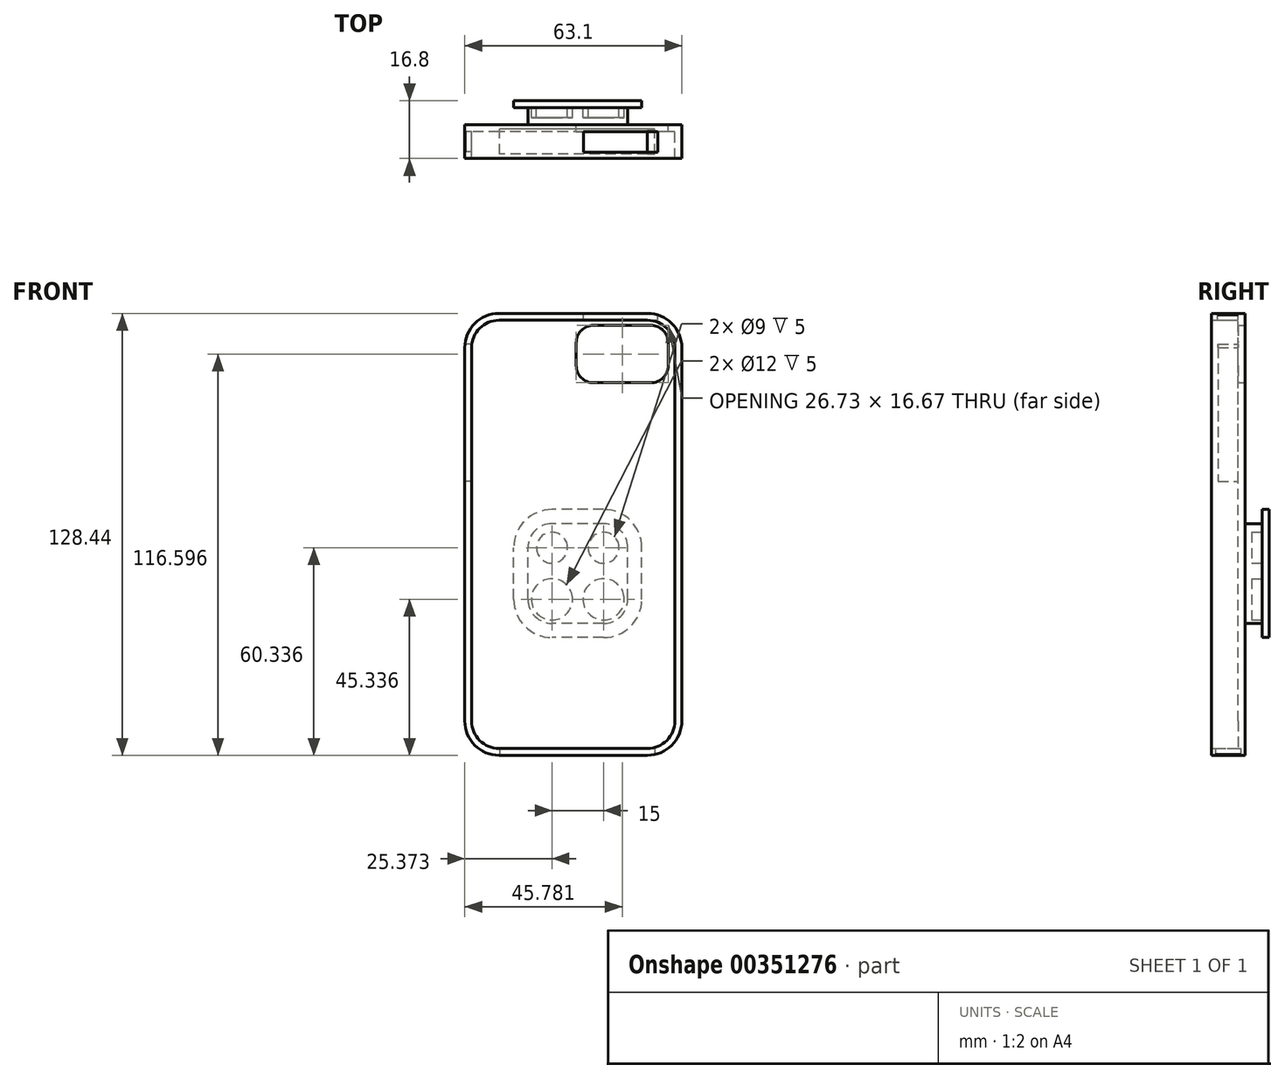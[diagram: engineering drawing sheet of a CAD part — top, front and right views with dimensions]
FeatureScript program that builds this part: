
annotation { "Feature Type Name" : "Feature", "Feature Type Description" : "" }
export const myFeature = defineFeature(function(context is Context, id is Id, definition is map)
    precondition{}
    {
        {
            var Q0;
            Q0=qCreatedBy(makeId("Front.planeOp"),FACE);
            var sketch = newSketch(context, id + "F0", { "sketchPlane" : qUnion([Q0])});
            skLineSegment(sketch, "E0.bottom", {"start": v(19.77, -64.98) * mm, "end": v(-23.33, -64.98) * mm});
            skLineSegment(sketch, "E0.top", {"start": v(19.77, 59.46) * mm, "end": v(-23.33, 59.46) * mm});
            skLineSegment(sketch, "E0.left", {"start": v(27.77, -56.98) * mm, "end": v(27.77, 51.46) * mm});
            skLineSegment(sketch, "E0.right", {"start": v(-31.33, -56.98) * mm, "end": v(-31.33, 51.46) * mm});
            skPoint(sketch, "E0.middle", {"position": v(0, 0) * mm});
            skArc(sketch, "E1.filletArc", {"start": v(-23.33, 59.46) * mm, "mid": v(-28.98, 57.12) * mm, "end": v(-31.33, 51.46) * mm});
            skArc(sketch, "E2.filletArc", {"start": v(27.77, 51.46) * mm, "mid": v(25.43, 57.12) * mm, "end": v(19.77, 59.46) * mm});
            skArc(sketch, "E3.filletArc", {"start": v(19.77, -64.98) * mm, "mid": v(25.43, -62.63) * mm, "end": v(27.77, -56.98) * mm});
            skArc(sketch, "E4.filletArc", {"start": v(-31.33, -56.98) * mm, "mid": v(-28.98, -62.63) * mm, "end": v(-23.33, -64.98) * mm});
            skSolve(sketch);
        }
        {
            var Q0;
            Q0 = qSketchRegion(id + "F0", true);
            extrude(context, id + "F1", {"entities" : qUnion([Q0]), "depth" : 7.8 * mm});
        }
        {
            var Q0;
            Q0=makeQuery(id+"F1.opExtrude","CAP_FACE",FACE,{"disambiguationData":[OSD([sQuery(id+"F0.wireOp",EDGE,"E0.bottom"),sQuery(id+"F0.wireOp",EDGE,"E0.top"),sQuery(id+"F0.wireOp",EDGE,"E0.left"),sQuery(id+"F0.wireOp",EDGE,"E0.right"),sQuery(id+"F0.wireOp",EDGE,"E1.filletArc"),sQuery(id+"F0.wireOp",EDGE,"E2.filletArc"),sQuery(id+"F0.wireOp",EDGE,"E3.filletArc"),sQuery(id+"F0.wireOp",EDGE,"E4.filletArc")])],"isStart":false});
            shell(context, id + "F2", {"entities" : qUnion([Q0]), "thickness" : 2 * mm, "oppositeDirection" : true});
        }
        {
            var Q0;
            Q0=makeQuery(id+"F1.opExtrude","CAP_FACE",FACE,{"disambiguationData":[OSD([sQuery(id+"F0.wireOp",EDGE,"E0.bottom"),sQuery(id+"F0.wireOp",EDGE,"E0.top"),sQuery(id+"F0.wireOp",EDGE,"E0.left"),sQuery(id+"F0.wireOp",EDGE,"E0.right"),sQuery(id+"F0.wireOp",EDGE,"E1.filletArc"),sQuery(id+"F0.wireOp",EDGE,"E2.filletArc"),sQuery(id+"F0.wireOp",EDGE,"E3.filletArc"),sQuery(id+"F0.wireOp",EDGE,"E4.filletArc")])],"isStart":true});
            var sketch = newSketch(context, id + "F3", { "sketchPlane" : qUnion([Q0])});
            skLineSegment(sketch, "E5.bottom", {"start": v(-20.82, 57.95) * mm, "end": v(-4.09, 57.95) * mm});
            skLineSegment(sketch, "E5.top", {"start": v(-20.82, 41.28) * mm, "end": v(-4.09, 41.28) * mm});
            skLineSegment(sketch, "E5.left", {"start": v(-25.82, 52.95) * mm, "end": v(-25.82, 46.28) * mm});
            skLineSegment(sketch, "E5.right", {"start": v(0.91, 52.95) * mm, "end": v(0.91, 46.28) * mm});
            skArc(sketch, "E6.filletArc", {"start": v(-20.82, 57.95) * mm, "mid": v(-24.35, 56.49) * mm, "end": v(-25.82, 52.95) * mm});
            skArc(sketch, "E7.filletArc", {"start": v(0.91, 52.95) * mm, "mid": v(-0.55, 56.49) * mm, "end": v(-4.09, 57.95) * mm});
            skArc(sketch, "E8.filletArc", {"start": v(-4.09, 41.28) * mm, "mid": v(-0.55, 42.74) * mm, "end": v(0.91, 46.28) * mm});
            skArc(sketch, "E9.filletArc", {"start": v(-25.82, 46.28) * mm, "mid": v(-24.35, 42.74) * mm, "end": v(-20.82, 41.28) * mm});
            skSolve(sketch);
        }
        {
            var Q0;
            Q0 = qSketchRegion(id + "F3", true);
            extrude(context, id + "F4", {"entities" : qUnion([Q0]), "operationType" : NewBodyOperationType.REMOVE, "endBound" : BoundingType.THROUGH_ALL, "oppositeDirection" : true, "depth" : 25 * mm});
        }
        {
            var Q0;
            Q0=makeQuery(id+"F1.opExtrude","SWEPT_FACE",FACE,{"disambiguationData":[OSD([sQuery(id+"F0.wireOp",EDGE,"E0.bottom")])]});
            var sketch = newSketch(context, id + "F5", { "sketchPlane" : qUnion([Q0])});
            skLineSegment(sketch, "E10.bottom", {"start": v(21.93, 6.55) * mm, "end": v(-23.15, 6.55) * mm});
            skLineSegment(sketch, "E10.top", {"start": v(21.93, -0.76) * mm, "end": v(-23.15, -0.76) * mm});
            skLineSegment(sketch, "E10.left", {"start": v(21.93, 6.55) * mm, "end": v(21.93, -0.76) * mm});
            skLineSegment(sketch, "E10.right", {"start": v(-23.15, 6.55) * mm, "end": v(-23.15, -0.76) * mm});
            skPoint(sketch, "E10.middle", {"position": v(-0.6, 2.9) * mm});
            skSolve(sketch);
        }
        {
            var Q0;
            Q0 = qSketchRegion(id + "F5", true);
            extrude(context, id + "F6", {"entities" : qUnion([Q0]), "operationType" : NewBodyOperationType.REMOVE, "oppositeDirection" : true, "depth" : 2 * mm});
        }
        {
            var Q0;
            Q0=makeQuery(id+"F1.opExtrude","SWEPT_FACE",FACE,{"disambiguationData":[OSD([sQuery(id+"F0.wireOp",EDGE,"E0.right")])]});
            var sketch = newSketch(context, id + "F7", { "sketchPlane" : qUnion([Q0])});
            skLineSegment(sketch, "E11", {"start": v(0, 52.52) * mm, "end": v(5.83, 52.52) * mm});
            skLineSegment(sketch, "E12", {"start": v(5.83, 52.52) * mm, "end": v(5.83, 12.61) * mm});
            skLineSegment(sketch, "E13", {"start": v(5.83, 12.61) * mm, "end": v(0, 12.61) * mm});
            skLineSegment(sketch, "E14", {"start": v(0, 12.61) * mm, "end": v(0, 52.52) * mm});
            skSolve(sketch);
        }
        {
            var Q0;
            Q0 = qSketchRegion(id + "F7", true);
            extrude(context, id + "F8", {"entities" : qUnion([Q0]), "operationType" : NewBodyOperationType.REMOVE, "oppositeDirection" : true, "depth" : 2 * mm});
        }
        {
            var Q0;
            Q0=makeQuery(id+"F1.opExtrude","SWEPT_FACE",FACE,{"disambiguationData":[OSD([sQuery(id+"F0.wireOp",EDGE,"E0.top")])]});
            var sketch = newSketch(context, id + "F9", { "sketchPlane" : qUnion([Q0])});
            skLineSegment(sketch, "E15", {"start": v(22.85, 0) * mm, "end": v(22.85, -5.94) * mm});
            skLineSegment(sketch, "E16", {"start": v(22.85, -5.94) * mm, "end": v(1.22, -5.94) * mm});
            skLineSegment(sketch, "E17", {"start": v(1.22, -5.94) * mm, "end": v(1.22, 0) * mm});
            skLineSegment(sketch, "E18", {"start": v(1.22, 0) * mm, "end": v(22.85, 0) * mm});
            skSolve(sketch);
        }
        {
            var Q0;
            Q0 = qSketchRegion(id + "F9", true);
            extrude(context, id + "F10", {"entities" : qUnion([Q0]), "operationType" : NewBodyOperationType.REMOVE, "oppositeDirection" : true, "depth" : 2 * mm});
        }
        {
            var Q0;
            Q0=makeQuery(id+"F1.opExtrude","CAP_FACE",FACE,{"disambiguationData":[OSD([sQuery(id+"F0.wireOp",EDGE,"E0.bottom"),sQuery(id+"F0.wireOp",EDGE,"E0.top"),sQuery(id+"F0.wireOp",EDGE,"E0.left"),sQuery(id+"F0.wireOp",EDGE,"E0.right"),sQuery(id+"F0.wireOp",EDGE,"E1.filletArc"),sQuery(id+"F0.wireOp",EDGE,"E2.filletArc"),sQuery(id+"F0.wireOp",EDGE,"E3.filletArc"),sQuery(id+"F0.wireOp",EDGE,"E4.filletArc")])],"isStart":true});
            var sketch = newSketch(context, id + "F11", { "sketchPlane" : qUnion([Q0])});
            skPoint(sketch, "E19.startSnap0", {"position": v(-29.77, -2.76) * mm});
            skSolve(sketch);
        }
        {
            var Q0;
            Q0=makeQuery(id+"F11.imprint","IMPRINT",FACE,{"disambiguationData":[TD([[makeQuery(id+"F11.imprint","IMPRINT",EDGE,{"derivedFrom":makeQuery(id+"F1.opExtrude","CAP_EDGE",EDGE,{"disambiguationData":[OSD([sQuery(id+"F0.wireOp",EDGE,"E0.bottom")])],"isStart":true})}),1.0]])]});
            var sketch = newSketch(context, id + "F12", { "sketchPlane" : qUnion([Q0])});
            skLineSegment(sketch, "E20.bottom", {"start": v(-7.04, -28.64) * mm, "end": v(7.96, -28.64) * mm});
            skLineSegment(sketch, "E20.top", {"start": v(-7.04, 0.36) * mm, "end": v(7.96, 0.36) * mm});
            skLineSegment(sketch, "E20.left", {"start": v(-14.04, -21.64) * mm, "end": v(-14.04, -6.64) * mm});
            skLineSegment(sketch, "E20.right", {"start": v(14.96, -21.64) * mm, "end": v(14.96, -6.64) * mm});
            skPoint(sketch, "E21.visualSharp", {"position": v(-14.04, 0.36) * mm});
            skArc(sketch, "E21.filletArc", {"start": v(-7.04, 0.36) * mm, "mid": v(-12, -1.7) * mm, "end": v(-14.04, -6.64) * mm});
            skPoint(sketch, "E22.visualSharp", {"position": v(14.96, -28.64) * mm});
            skArc(sketch, "E22.filletArc", {"start": v(7.96, -28.64) * mm, "mid": v(12.9, -26.6) * mm, "end": v(14.96, -21.64) * mm});
            skPoint(sketch, "E23.visualSharp", {"position": v(14.96, 0.36) * mm});
            skArc(sketch, "E23.filletArc", {"start": v(14.96, -6.64) * mm, "mid": v(12.9, -1.7) * mm, "end": v(7.96, 0.36) * mm});
            skPoint(sketch, "E24.visualSharp", {"position": v(-14.04, -28.64) * mm});
            skArc(sketch, "E24.filletArc", {"start": v(-14.04, -21.64) * mm, "mid": v(-12, -26.6) * mm, "end": v(-7.04, -28.64) * mm});
            skSolve(sketch);
        }
        {
            var Q0;
            Q0 = qSketchRegion(id + "F12", true);
            extrude(context, id + "F13", {"entities" : qUnion([Q0]), "depth" : 7 * mm});
        }
        {
            var Q0;
            Q0=makeQuery(id+"F13.opExtrude","CAP_FACE",FACE,{"disambiguationData":[OSD([sQuery(id+"F12.wireOp",EDGE,"E20.bottom"),sQuery(id+"F12.wireOp",EDGE,"E20.top"),sQuery(id+"F12.wireOp",EDGE,"E20.left"),sQuery(id+"F12.wireOp",EDGE,"E20.right")])],"isStart":false});
            var sketch = newSketch(context, id + "F14", { "sketchPlane" : qUnion([Q0])});
            skCircle(sketch, "E25", {"center": v(-7.04, -6.64) * mm, "radius": 4.5 * mm});
            skCircle(sketch, "E26", {"center": v(7.96, -6.64) * mm, "radius": 4.5 * mm});
            skCircle(sketch, "E27", {"center": v(-7.04, -21.64) * mm, "radius": 6 * mm});
            skCircle(sketch, "E28", {"center": v(7.96, -21.64) * mm, "radius": 6 * mm});
            skSolve(sketch);
        }
        {
            var Q0;
            Q0=makeQuery(id+"F14.imprint","IMPRINT",FACE,{"disambiguationData":[TD([[makeQuery(id+"F14.imprint","IMPRINT",EDGE,{"derivedFrom":sQuery(id+"F14.wireOp",EDGE,"E25")}),-1.0]])]});
            var sketch = newSketch(context, id + "F15", { "sketchPlane" : qUnion([Q0])});
            skArc(sketch, "E29.0", {"start": v(-7.04, 4.46) * mm, "mid": v(-14.9, 1.2) * mm, "end": v(-18.14, -6.64) * mm});
            skLineSegment(sketch, "E29.1", {"start": v(-18.14, -21.64) * mm, "end": v(-18.14, -6.64) * mm});
            skLineSegment(sketch, "E29.2", {"start": v(-7.04, 4.46) * mm, "end": v(7.96, 4.46) * mm});
            skArc(sketch, "E29.3", {"start": v(-18.14, -21.64) * mm, "mid": v(-14.9, -29.5) * mm, "end": v(-7.04, -32.74) * mm});
            skArc(sketch, "E29.4", {"start": v(19.06, -6.64) * mm, "mid": v(15.8, 1.2) * mm, "end": v(7.96, 4.46) * mm});
            skLineSegment(sketch, "E29.5", {"start": v(19.06, -21.64) * mm, "end": v(19.06, -6.64) * mm});
            skArc(sketch, "E29.6", {"start": v(7.96, -32.74) * mm, "mid": v(15.8, -29.5) * mm, "end": v(19.06, -21.64) * mm});
            skLineSegment(sketch, "E29.7", {"start": v(-7.04, -32.74) * mm, "end": v(7.96, -32.74) * mm});
            skSolve(sketch);
        }
        {
            var Q0;
            Q0=makeQuery(id+"F15.imprint","IMPRINT",FACE,{"disambiguationData":[TD([[makeQuery(id+"F15.imprint","IMPRINT",EDGE,{"derivedFrom":sQuery(id+"F15.wireOp",EDGE,"E29.0")}),1.0]])]});
            extrude(context, id + "F16", {"entities" : qUnion([Q0]), "operationType" : NewBodyOperationType.ADD, "oppositeDirection" : true, "depth" : 2 * mm});
        }
        {
            var Q0;
            Q0 = qSketchRegion(id + "F14", true);
            extrude(context, id + "F17", {"entities" : qUnion([Q0]), "operationType" : NewBodyOperationType.REMOVE, "endBound" : BoundingType.THROUGH_ALL, "depth" : 7 * mm});
        }
        {
            var Q0;
            Q0=makeQuery(id+"F14.imprint","IMPRINT",FACE,{"disambiguationData":[TD([[makeQuery(id+"F14.imprint","IMPRINT",EDGE,{"derivedFrom":sQuery(id+"F14.wireOp",EDGE,"E26")}),1.0]])]});
            var Q1;
            Q1=makeQuery(id+"F14.imprint","IMPRINT",FACE,{"disambiguationData":[TD([[makeQuery(id+"F14.imprint","IMPRINT",EDGE,{"derivedFrom":sQuery(id+"F14.wireOp",EDGE,"E25")}),1.0]])]});
            var Q2;
            Q2=makeQuery(id+"F14.imprint","IMPRINT",FACE,{"disambiguationData":[TD([[makeQuery(id+"F14.imprint","IMPRINT",EDGE,{"derivedFrom":sQuery(id+"F14.wireOp",EDGE,"E27")}),1.0]])]});
            var Q3;
            Q3=makeQuery(id+"F14.imprint","IMPRINT",FACE,{"disambiguationData":[TD([[makeQuery(id+"F14.imprint","IMPRINT",EDGE,{"derivedFrom":sQuery(id+"F14.wireOp",EDGE,"E28")}),1.0]])]});
            extrude(context, id + "F18", {"entities" : qUnion([Q0, Q1, Q2, Q3]), "operationType" : NewBodyOperationType.REMOVE, "oppositeDirection" : true, "depth" : 5 * mm});
        }
    });
